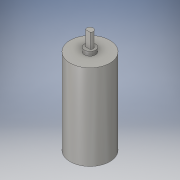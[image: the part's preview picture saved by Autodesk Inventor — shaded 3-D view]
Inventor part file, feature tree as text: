
AUTODESK INVENTOR PART (.ipt)
format: ipt  version: 2016 (Build 200138000, 138)  size: 111,616 bytes
history: native  units: in
note: dims shown in document units (in); Inventor stores cm internally (conversion verified against a paired STEP export)
features: extrude x4, sketch x4
ambient origin geometry x8: Origin, YZ Plane, XZ Plane, XY Plane, X Axis, Y Axis, Z Axis, Center Point
bodies: Solid1 (feature_tree)
feature tree (8):
  extrude  "Extrusion1"  Depth=2.1161in TaperAngle=0.0deg
  extrude  "Extrusion2"  Depth=0.47in TaperAngle=0.0deg
  extrude  "Extrusion3"  Depth=0.2725in
  extrude  "Extrusion4"  Depth=0.1in
  sketch  "Sketch1"  dims[d0=0.9843in d1=2.1161in d2=0.0in]
  sketch  "Sketch2"  dims[d3=0.1575in d4=0.47in d5=0.0in]
  sketch  "Sketch3"  dims[d7=0.4331in d8=0.0in d9=0.2725in]
  sketch  "Sketch4"  dims[d10=0.1in d11=0.0in d12=0.0515in]
